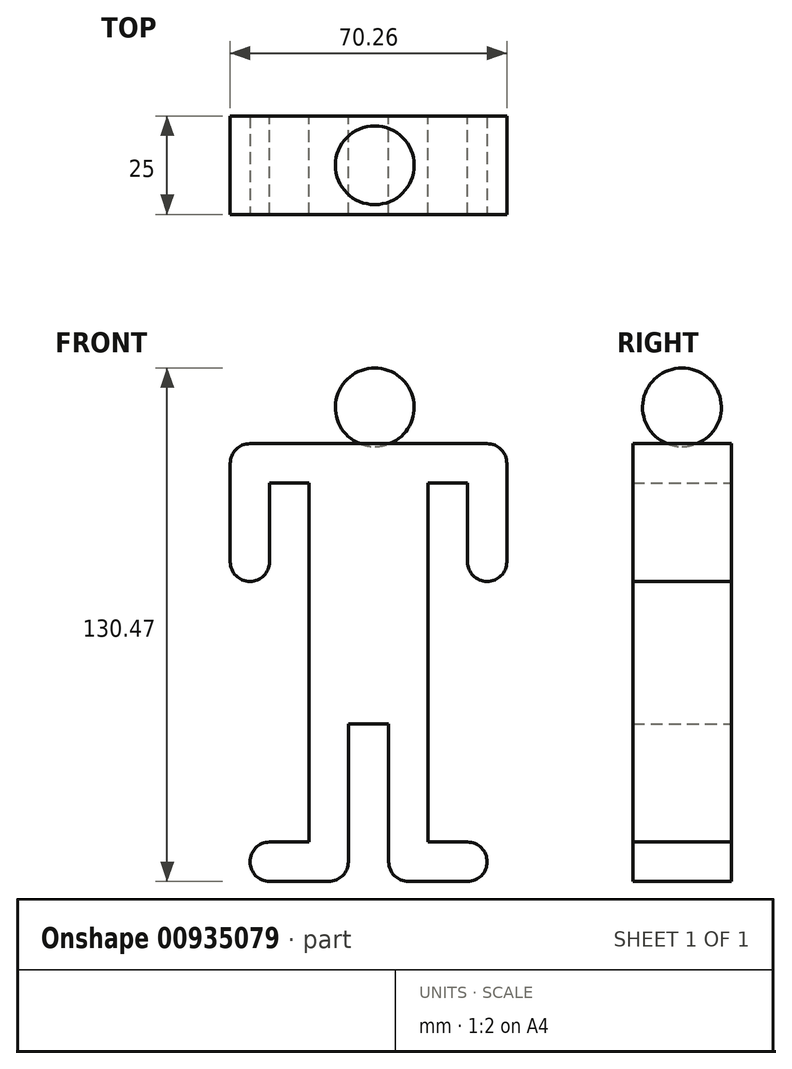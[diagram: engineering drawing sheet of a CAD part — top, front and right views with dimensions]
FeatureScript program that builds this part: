
annotation { "Feature Type Name" : "Feature", "Feature Type Description" : "" }
export const myFeature = defineFeature(function(context is Context, id is Id, definition is map)
    precondition{}
    {
        {
            var Q0;
            Q0=qCreatedBy(makeId("Front.planeOp"),FACE);
            var sketch = newSketch(context, id + "F0", { "sketchPlane" : qUnion([Q0])});
            skLineSegment(sketch, "E0.bottom", {"start": v(-16.71, 42.1) * mm, "end": v(13.55, 42.1) * mm});
            skLineSegment(sketch, "E0.top", {"start": v(-16.71, -29.1) * mm, "end": v(13.55, -29.1) * mm});
            skLineSegment(sketch, "E0.left", {"start": v(-16.71, 42.1) * mm, "end": v(-16.71, -29.1) * mm});
            skLineSegment(sketch, "E0.right", {"start": v(13.55, 42.1) * mm, "end": v(13.55, -29.1) * mm});
            skSolve(sketch);
        }
        {
            var Q0;
            Q0 = qSketchRegion(id + "F0", true);
            extrude(context, id + "F1", {"entities" : qUnion([Q0]), "depth" : 12.5 * mm, "offsetDistance" : 25 * mm, "hasSecondDirection" : true, "secondDirectionOppositeDirection" : true, "secondDirectionDepth" : 12.5 * mm});
        }
        {
            var Q0;
            Q0=qCreatedBy(makeId("Front.planeOp"),FACE);
            var sketch = newSketch(context, id + "F2", { "sketchPlane" : qUnion([Q0])});
            skLineSegment(sketch, "E1", {"start": v(0, 61.36) * mm, "end": v(0, 41.36) * mm});
            skArc(sketch, "E2", {"start": v(0, 41.36) * mm, "mid": v(10, 51.36) * mm, "end": v(0, 61.36) * mm});
            skSolve(sketch);
        }
        {
            var Q0;
            Q0 = qSketchRegion(id + "F2", true);
            var Q1;
            Q1=sQuery(id+"F2.wireOp",EDGE,"E1");
            revolve(context, id + "F3", {"surfaceOperationType" : NewSurfaceOperationType.NEW, "entities" : qUnion([Q0]), "axis" : qUnion([Q1]), "revolveType" : RevolveType.FULL});
        }
        {
            var Q0;
            Q0=qCreatedBy(makeId("Front.planeOp"),FACE);
            var sketch = newSketch(context, id + "F4", { "sketchPlane" : qUnion([Q0])});
            skLineSegment(sketch, "E3.bottom", {"start": v(3.55, -29.1) * mm, "end": v(13.55, -29.1) * mm});
            skLineSegment(sketch, "E3.top", {"start": v(3.55, -69.1) * mm, "end": v(13.55, -69.1) * mm});
            skLineSegment(sketch, "E3.left", {"start": v(3.55, -29.1) * mm, "end": v(3.55, -69.1) * mm});
            skLineSegment(sketch, "E3.right", {"start": v(13.55, -29.1) * mm, "end": v(13.55, -69.1) * mm});
            skLineSegment(sketch, "E4.bottom", {"start": v(28.55, -59.1) * mm, "end": v(13.55, -59.1) * mm});
            skLineSegment(sketch, "E4.top", {"start": v(28.55, -69.1) * mm, "end": v(13.55, -69.1) * mm});
            skLineSegment(sketch, "E4.left", {"start": v(28.55, -59.1) * mm, "end": v(28.55, -69.1) * mm});
            skLineSegment(sketch, "E4.right", {"start": v(13.55, -59.1) * mm, "end": v(13.55, -69.1) * mm});
            skLineSegment(sketch, "E5.bottom", {"start": v(-6.71, -29.1) * mm, "end": v(-16.71, -29.1) * mm});
            skLineSegment(sketch, "E5.top", {"start": v(-6.71, -69.1) * mm, "end": v(-16.71, -69.1) * mm});
            skLineSegment(sketch, "E5.left", {"start": v(-6.71, -29.1) * mm, "end": v(-6.71, -69.1) * mm});
            skLineSegment(sketch, "E5.right", {"start": v(-16.71, -29.1) * mm, "end": v(-16.71, -69.1) * mm});
            skLineSegment(sketch, "E6.bottom", {"start": v(-16.71, -59.1) * mm, "end": v(-31.71, -59.1) * mm});
            skLineSegment(sketch, "E6.top", {"start": v(-16.71, -69.1) * mm, "end": v(-31.71, -69.1) * mm});
            skLineSegment(sketch, "E6.left", {"start": v(-16.71, -59.1) * mm, "end": v(-16.71, -69.1) * mm});
            skLineSegment(sketch, "E6.right", {"start": v(-31.71, -59.1) * mm, "end": v(-31.71, -69.1) * mm});
            skLineSegment(sketch, "E7.bottom", {"start": v(-16.71, 42.1) * mm, "end": v(-36.71, 42.1) * mm});
            skLineSegment(sketch, "E7.top", {"start": v(-16.71, 32.1) * mm, "end": v(-36.71, 32.1) * mm});
            skLineSegment(sketch, "E7.left", {"start": v(-16.71, 42.1) * mm, "end": v(-16.71, 32.1) * mm});
            skLineSegment(sketch, "E7.right", {"start": v(-36.71, 42.1) * mm, "end": v(-36.71, 32.1) * mm});
            skLineSegment(sketch, "E8.bottom", {"start": v(-36.71, 32.1) * mm, "end": v(-26.71, 32.1) * mm});
            skLineSegment(sketch, "E8.top", {"start": v(-36.71, 7.1) * mm, "end": v(-26.71, 7.1) * mm});
            skLineSegment(sketch, "E8.left", {"start": v(-36.71, 32.1) * mm, "end": v(-36.71, 7.1) * mm});
            skLineSegment(sketch, "E8.right", {"start": v(-26.71, 32.1) * mm, "end": v(-26.71, 7.1) * mm});
            skLineSegment(sketch, "E9.bottom", {"start": v(13.55, 42.1) * mm, "end": v(33.55, 42.1) * mm});
            skLineSegment(sketch, "E9.top", {"start": v(13.55, 32.1) * mm, "end": v(33.55, 32.1) * mm});
            skLineSegment(sketch, "E9.left", {"start": v(13.55, 42.1) * mm, "end": v(13.55, 32.1) * mm});
            skLineSegment(sketch, "E9.right", {"start": v(33.55, 42.1) * mm, "end": v(33.55, 32.1) * mm});
            skLineSegment(sketch, "E10.bottom", {"start": v(33.55, 32.1) * mm, "end": v(23.55, 32.1) * mm});
            skLineSegment(sketch, "E10.top", {"start": v(33.55, 7.1) * mm, "end": v(23.55, 7.1) * mm});
            skLineSegment(sketch, "E10.left", {"start": v(33.55, 32.1) * mm, "end": v(33.55, 7.1) * mm});
            skLineSegment(sketch, "E10.right", {"start": v(23.55, 32.1) * mm, "end": v(23.55, 7.1) * mm});
            skSolve(sketch);
        }
        {
            var Q0;
            Q0 = qSketchRegion(id + "F4", true);
            extrude(context, id + "F5", {"entities" : qUnion([Q0]), "operationType" : NewBodyOperationType.ADD, "depth" : 12.5 * mm, "offsetDistance" : 25 * mm, "hasSecondDirection" : true, "secondDirectionOppositeDirection" : true, "secondDirectionDepth" : 12.5 * mm});
        }
        {
            var Q0;
            Q0=makeQuery(id+"F5.opExtrude","SWEPT_EDGE",EDGE,{"disambiguationData":[OSD([sQuery(id+"F4.wireOp",EDGE,"E7.bottom"),sQuery(id+"F4.wireOp",EDGE,"E7.right")])]});
            var Q1;
            Q1=makeQuery(id+"F5.opExtrude","SWEPT_EDGE",EDGE,{"disambiguationData":[OSD([sQuery(id+"F4.wireOp",EDGE,"E9.bottom"),sQuery(id+"F4.wireOp",EDGE,"E9.right")])]});
            var Q2;
            Q2=makeQuery(id+"F5.opExtrude","SWEPT_EDGE",EDGE,{"disambiguationData":[OSD([sQuery(id+"F4.wireOp",EDGE,"E5.top"),sQuery(id+"F4.wireOp",EDGE,"E5.left")])]});
            var Q3;
            Q3=makeQuery(id+"F5.opExtrude","SWEPT_EDGE",EDGE,{"disambiguationData":[OSD([sQuery(id+"F4.wireOp",EDGE,"E3.top"),sQuery(id+"F4.wireOp",EDGE,"E3.left")])]});
            var Q4;
            Q4=makeQuery(id+"F5.opExtrude","SWEPT_EDGE",EDGE,{"disambiguationData":[OSD([sQuery(id+"F4.wireOp",EDGE,"E8.top"),sQuery(id+"F4.wireOp",EDGE,"E8.left")])]});
            var Q5;
            Q5=makeQuery(id+"F5.opExtrude","SWEPT_EDGE",EDGE,{"disambiguationData":[OSD([sQuery(id+"F4.wireOp",EDGE,"E10.top"),sQuery(id+"F4.wireOp",EDGE,"E10.right")])]});
            var Q6;
            Q6=makeQuery(id+"F5.opExtrude","SWEPT_EDGE",EDGE,{"disambiguationData":[OSD([sQuery(id+"F4.wireOp",EDGE,"E6.top"),sQuery(id+"F4.wireOp",EDGE,"E6.right")])]});
            var Q7;
            Q7=makeQuery(id+"F5.opExtrude","SWEPT_EDGE",EDGE,{"disambiguationData":[OSD([sQuery(id+"F4.wireOp",EDGE,"E6.bottom"),sQuery(id+"F4.wireOp",EDGE,"E6.right")])]});
            var Q8;
            Q8=makeQuery(id+"F5.opExtrude","SWEPT_EDGE",EDGE,{"disambiguationData":[OSD([sQuery(id+"F4.wireOp",EDGE,"E8.top"),sQuery(id+"F4.wireOp",EDGE,"E8.right")])]});
            var Q9;
            Q9=makeQuery(id+"F5.opExtrude","SWEPT_EDGE",EDGE,{"disambiguationData":[OSD([sQuery(id+"F4.wireOp",EDGE,"E10.top"),sQuery(id+"F4.wireOp",EDGE,"E10.left")])]});
            var Q10;
            Q10=makeQuery(id+"F5.opExtrude","SWEPT_EDGE",EDGE,{"disambiguationData":[OSD([sQuery(id+"F4.wireOp",EDGE,"E4.bottom"),sQuery(id+"F4.wireOp",EDGE,"E4.left")])]});
            var Q11;
            Q11=makeQuery(id+"F5.opExtrude","SWEPT_EDGE",EDGE,{"disambiguationData":[OSD([sQuery(id+"F4.wireOp",EDGE,"E4.top"),sQuery(id+"F4.wireOp",EDGE,"E4.left")])]});
            fillet(context, id + "F6", {"entities" : qUnion([Q0, Q1, Q2, Q3, Q4, Q5, Q6, Q7, Q8, Q9, Q10, Q11]), "radius" : 5 * mm, "tangentPropagation" : true, "allowEdgeOverflow" : false});
        }
    });
